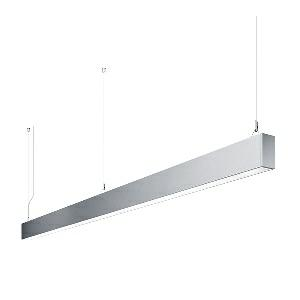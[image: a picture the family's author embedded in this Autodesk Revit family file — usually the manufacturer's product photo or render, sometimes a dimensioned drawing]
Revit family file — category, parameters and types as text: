
# Revit family: idoo_line_-_ilp_6000_830_d_00805747_4aab
name_source: partatom
category: Lighting Fixtures
units: mm (PartAtom-declared; Revit-internal decimal feet)

## family parameters
Cut with Voids When Loaded = No
Host = Face
Light Source = No
Part Type = Normal
Room Calculation Point = No
Round Connector Dimension = Use Diameter
Shared = No

## types (1)
- IDOO.line - ILP 6000/830/D (1 x LED, 6000 lm, 3000K)
    Apparent Load = 46 VA
    Approval mark = CE
    CIE Flux Codes = 66 91 98 40 100
    Color Rendering = 80-89
    Color Temperature = 3000K
    Control Gear = Electronic ballast
    Default Elevation = 1800 mm
    Description = ILP 6000/830/D|Suspended luminaire|light source: LED|connected load: 220-240V, 50/60Hz|Power consumption: approx. 46 W|standby: approx. 0,15|luminous flux: 6000 lm|luminous efficacy: 130 lm/W|light distribution: Direct/indirect|direct ratio: approx. 40 %|colour temperature: Warm white, ca. 3000 K|color rendering index (CRI): >= 80|chromaticity tolerance:  3 SDCM|System of protection: IP 40|technology: Continuously dimmable|luminaire body|material: Sectional aluminium|colour: Silver|lamp cover: Acrylic (PMMA), Clear|mains lead: 2.00 m With free stranded wires|Fastening: Steel cable 0.3 - 0.7 m|glare control: Prism aperture|luminance(L65): <= 2700 cd/m|unified glare rating(4H 8H): <=  16|special features: DALI Load 1x, TouchDIM - dimming via standard switch, Flicker-free, Suitable as emergency lighting|
    Frequency = 50 Hz
    Height = 110 mm
    Lamp = 1 x LED
    Lamp Light Flux = 6000 lm
    Lamp count = 1
    Length = 2256 mm
    Luminous efficacy = 130 lm/W
    Manufacturer = Waldmann
    ModVariant = No
    Model = 00805747
    Mounting Place = Ceiling
    Mounting Type = Pendant
    Number of Poles = 1
    OnlyDefault = Yes
    Power Factor = 1
    Product Name = IDOO.line - ILP 6000/830/D
    Product group = Suspended luminaire
    ProductGroupID = 9
    Protection Class = Protection class I
    Protection Degree = IP 40
    RLX_Detail_Level = 1
    RLX_Emergency_Light_Flux = 0 lm
    RLX_Emergency_Type = 0
    RLX_Emergency_Type_DB = No
    RlxData = <blob elided: 23145 chars, md5=778bb0cf>
    Socket = socket
    Standby Power = 0 W
    System Light Flux = 6000 lm
    System Power = 46 W
    Type Comments = Product without accessories
    Type Image = 113294000-00692533.jpg
    URL = http://relux.com
    VarID = ---
    Voltage = 230 V
    Voltage Range = 220-240 V
    Weight = 0.00 kg
    Width = 60 mm  [stored 0.19685 ft]

note: [stored X ft] marks values corroborated as IEEE doubles in the binary element streams (Revit-internal decimal feet)

## geometry (parser evidence)
native form markers: Blend x4, Sweep x13
no freeform markers — native parametric forms only
